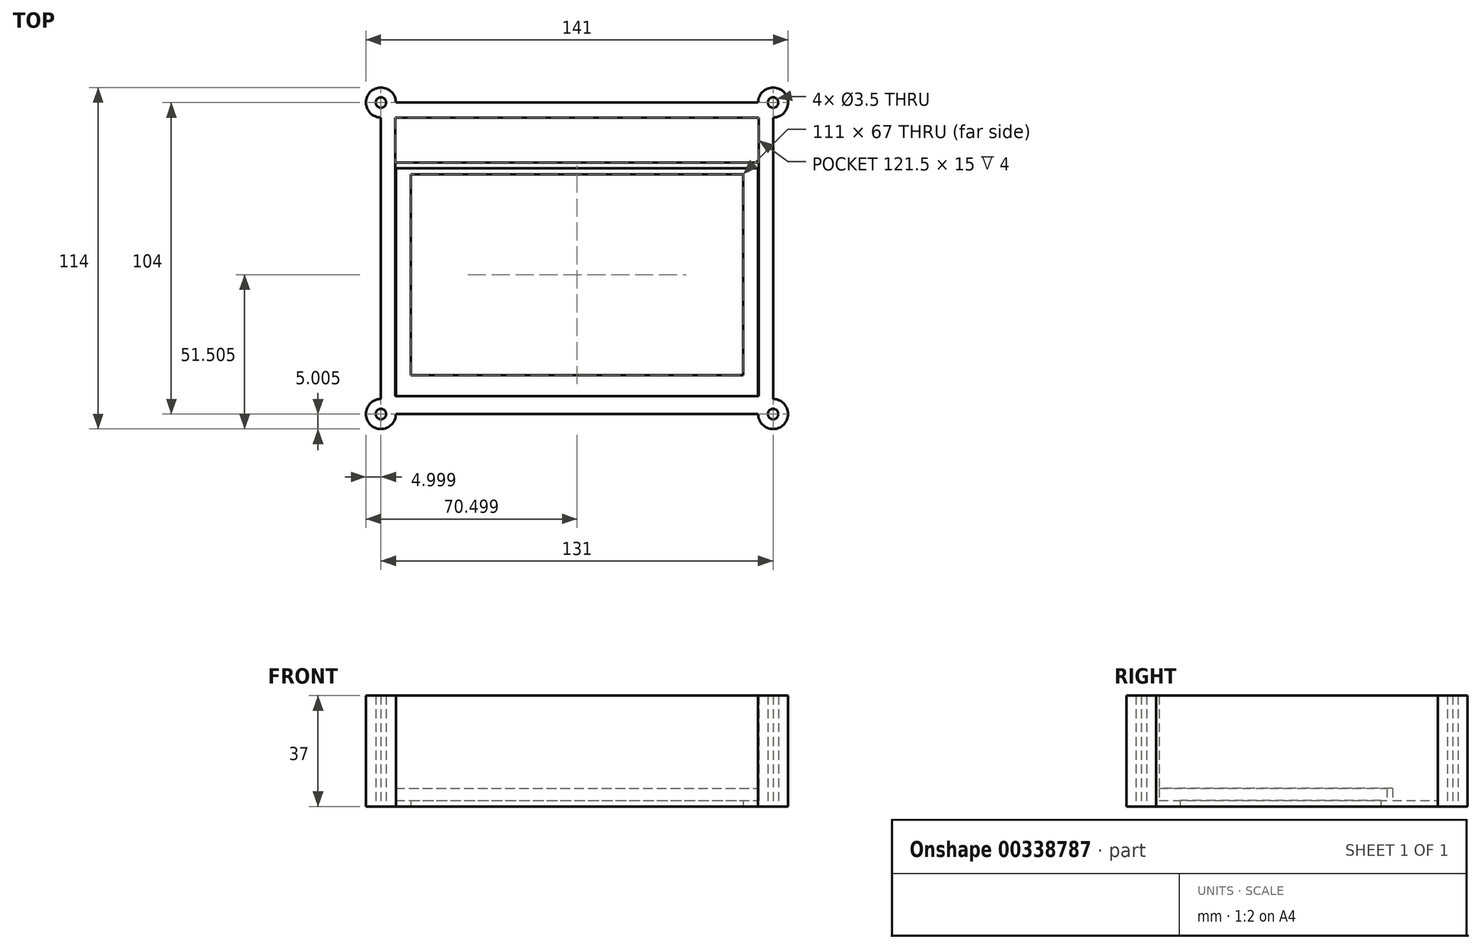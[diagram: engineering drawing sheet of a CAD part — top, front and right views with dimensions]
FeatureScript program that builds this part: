
annotation { "Feature Type Name" : "Feature", "Feature Type Description" : "" }
export const myFeature = defineFeature(function(context is Context, id is Id, definition is map)
    precondition{}
    {
        {
            var Q0;
            Q0=qCreatedBy(makeId("Top.planeOp"),FACE);
            var sketch = newSketch(context, id + "F0", { "sketchPlane" : qUnion([Q0])});
            skLineSegment(sketch, "E0.bottom", {"start": v(-69.33, -60.03) * mm, "end": v(51.67, -60.03) * mm});
            skLineSegment(sketch, "E0.top", {"start": v(-69.33, 15.97) * mm, "end": v(51.67, 15.97) * mm});
            skLineSegment(sketch, "E0.left", {"start": v(-69.33, -60.03) * mm, "end": v(-69.33, 15.97) * mm});
            skLineSegment(sketch, "E0.right", {"start": v(51.67, -60.03) * mm, "end": v(51.67, 15.97) * mm});
            skLineSegment(sketch, "E1.bottom", {"start": v(-64.33, 13.97) * mm, "end": v(46.67, 13.97) * mm});
            skLineSegment(sketch, "E1.top", {"start": v(-64.33, -53.03) * mm, "end": v(46.67, -53.03) * mm});
            skLineSegment(sketch, "E1.left", {"start": v(-64.33, 13.97) * mm, "end": v(-64.33, -53.03) * mm});
            skLineSegment(sketch, "E1.right", {"start": v(46.67, 13.97) * mm, "end": v(46.67, -53.03) * mm});
            skLineSegment(sketch, "E2.bottom", {"start": v(-69.58, 17.97) * mm, "end": v(51.92, 17.97) * mm});
            skLineSegment(sketch, "E2.top", {"start": v(-69.58, -60.03) * mm, "end": v(51.92, -60.03) * mm});
            skLineSegment(sketch, "E2.right", {"start": v(51.92, 17.97) * mm, "end": v(51.92, -60.03) * mm});
            skArc(sketch, "E3", {"start": v(-74.33, 42.97) * mm, "mid": v(-79.33, 37.97) * mm, "end": v(-74.33, 32.97) * mm});
            skLineSegment(sketch, "E4", {"start": v(-69.33, 37.97) * mm, "end": v(-69.33, 37.97) * mm});
            skArc(sketch, "E5", {"start": v(-74.33, -61.03) * mm, "mid": v(-77.87, -69.56) * mm, "end": v(-69.33, -66.03) * mm});
            skLineSegment(sketch, "E6", {"start": v(-69.33, -66.03) * mm, "end": v(-69.33, -66.03) * mm});
            skLineSegment(sketch, "E7", {"start": v(-69.33, -66.03) * mm, "end": v(51.67, -66.03) * mm});
            skLineSegment(sketch, "E8", {"start": v(-69.33, 37.97) * mm, "end": v(51.67, 37.97) * mm});
            skArc(sketch, "E9", {"start": v(-69.33, 37.97) * mm, "mid": v(-70.8, 41.51) * mm, "end": v(-74.33, 42.97) * mm});
            skLineSegment(sketch, "E10", {"start": v(56.67, 32.97) * mm, "end": v(56.67, 32.97) * mm});
            skArc(sketch, "E11", {"start": v(56.67, 32.97) * mm, "mid": v(60.2, 41.51) * mm, "end": v(51.67, 37.97) * mm});
            skArc(sketch, "E12", {"start": v(51.67, -66.03) * mm, "mid": v(60.2, -69.56) * mm, "end": v(56.67, -61.03) * mm});
            skCircle(sketch, "E13", {"center": v(-74.33, 37.97) * mm, "radius": 1.75 * mm});
            skCircle(sketch, "E14", {"center": v(56.67, 37.97) * mm, "radius": 1.75 * mm});
            skCircle(sketch, "E15", {"center": v(-74.33, -66.03) * mm, "radius": 1.75 * mm});
            skCircle(sketch, "E16", {"center": v(56.67, -66.03) * mm, "radius": 1.75 * mm});
            skLineSegment(sketch, "E17", {"start": v(56.67, 32.97) * mm, "end": v(56.67, -61.03) * mm});
            skLineSegment(sketch, "E18", {"start": v(56.67, 32.97) * mm, "end": v(-74.33, 32.97) * mm});
            skLineSegment(sketch, "E19", {"start": v(-74.33, 32.97) * mm, "end": v(-74.33, -61.03) * mm});
            skLineSegment(sketch, "E20", {"start": v(-69.58, 17.97) * mm, "end": v(-69.58, 32.97) * mm});
            skLineSegment(sketch, "E21", {"start": v(-69.58, 17.97) * mm, "end": v(-69.58, -60.03) * mm});
            skLineSegment(sketch, "E22", {"start": v(51.92, 17.97) * mm, "end": v(51.92, 32.97) * mm});
            skSolve(sketch);
        }
        {
            var Q0;
            Q0=makeQuery(id+"F0.imprint","IMPRINT",FACE,{"disambiguationData":[TD([[makeQuery(id+"F0.imprint","IMPRINT",EDGE,{"derivedFrom":sQuery(id+"F0.wireOp",EDGE,"E0.top")}),-1.0]])]});
            extrude(context, id + "F1", {"entities" : qUnion([Q0]), "depth" : 2 * mm});
        }
        {
            var Q0;
            Q0=makeQuery(id+"F0.imprint","IMPRINT",FACE,{"disambiguationData":[TD([[makeQuery(id+"F0.imprint","IMPRINT",EDGE,{"derivedFrom":sQuery(id+"F0.wireOp",EDGE,"E0.top")}),1.0]])]});
            extrude(context, id + "F2", {"entities" : qUnion([Q0]), "operationType" : NewBodyOperationType.ADD, "depth" : 6 * mm});
        }
        {
            var Q0;
            Q0=makeQuery(id+"F0.imprint","IMPRINT",FACE,{"disambiguationData":[TD([[makeQuery(id+"F0.imprint","IMPRINT",EDGE,{"derivedFrom":sQuery(id+"F0.wireOp",EDGE,"E2.bottom")}),1.0]])]});
            extrude(context, id + "F3", {"entities" : qUnion([Q0]), "operationType" : NewBodyOperationType.ADD, "depth" : 2 * mm});
        }
        {
            var Q0;
            {var subQ1=sQuery(id+"F0.wireOp",EDGE,"E3");Q0=makeQuery(id+"F0.imprint","IMPRINT",FACE,{"disambiguationData":[TD([[makeQuery(id+"F0.imprint","IMPRINT",EDGE,{"derivedFrom":subQ1}),1.0]])]});}
            var Q1;
            {var subQ5=sQuery(id+"F0.wireOp",EDGE,"E2.right");Q1=makeQuery(id+"F0.imprint","IMPRINT",FACE,{"disambiguationData":[TD([[makeQuery(id+"F0.imprint","IMPRINT",EDGE,{"derivedFrom":subQ5}),1.0]])]});}
            extrude(context, id + "F4", {"entities" : qUnion([Q0, Q1]), "operationType" : NewBodyOperationType.ADD, "depth" : 37 * mm});
        }
    });
